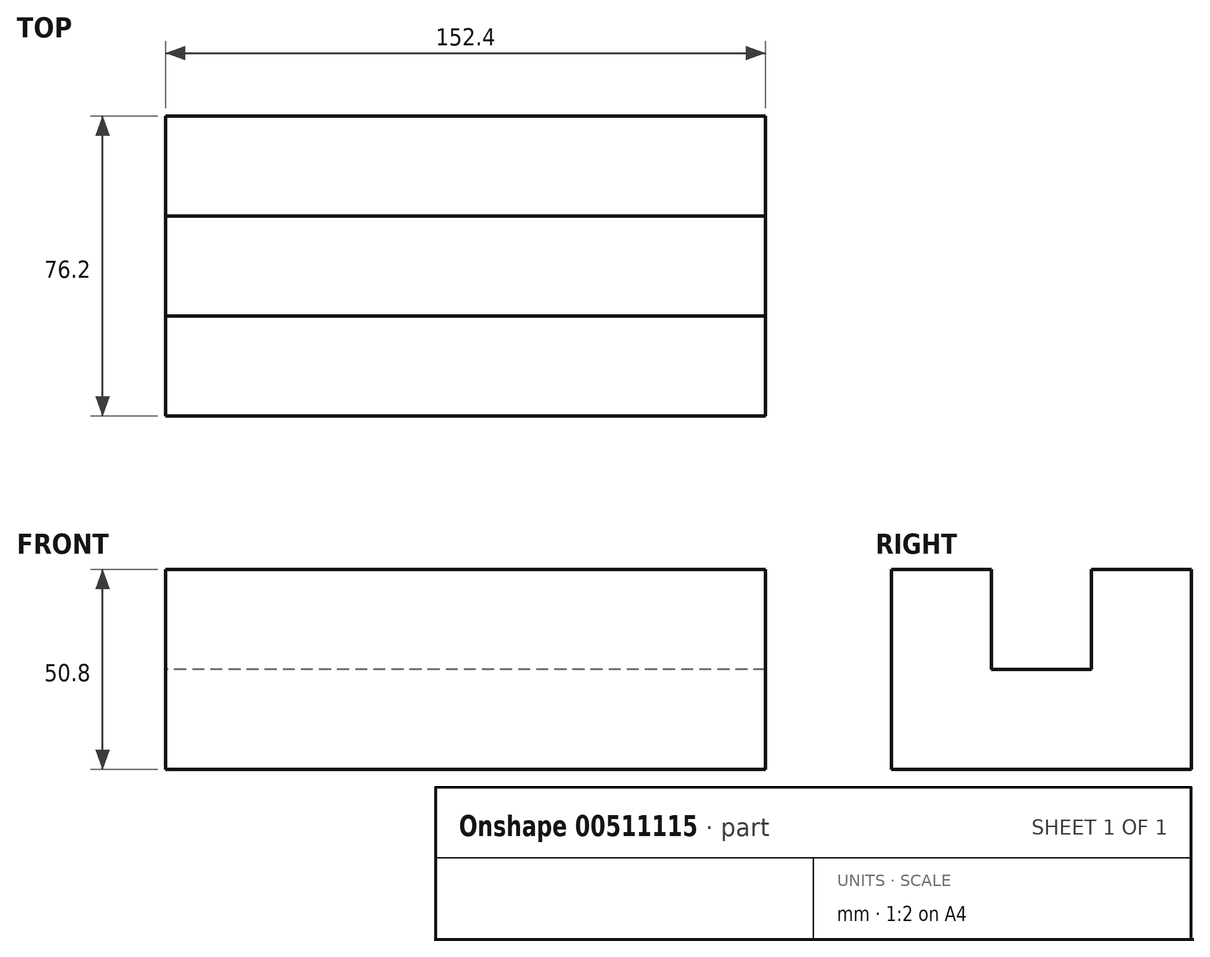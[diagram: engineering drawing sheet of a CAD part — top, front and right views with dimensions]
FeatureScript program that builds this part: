
annotation { "Feature Type Name" : "Feature", "Feature Type Description" : "" }
export const myFeature = defineFeature(function(context is Context, id is Id, definition is map)
    precondition{}
    {
        {
            var Q0;
            Q0=qCreatedBy(makeId("Right.planeOp"),FACE);
            var sketch = newSketch(context, id + "F0", { "sketchPlane" : qUnion([Q0])});
            skLineSegment(sketch, "E0", {"start": v(-40.6, 57.32) * mm, "end": v(-40.6, 6.52) * mm});
            skLineSegment(sketch, "E1", {"start": v(-40.6, 6.52) * mm, "end": v(35.6, 6.52) * mm});
            skLineSegment(sketch, "E2", {"start": v(35.6, 6.52) * mm, "end": v(35.6, 57.32) * mm});
            skLineSegment(sketch, "E3", {"start": v(35.6, 57.32) * mm, "end": v(10.2, 57.32) * mm});
            skLineSegment(sketch, "E4", {"start": v(10.2, 57.32) * mm, "end": v(10.2, 31.92) * mm});
            skLineSegment(sketch, "E5", {"start": v(10.2, 31.92) * mm, "end": v(-15.2, 31.92) * mm});
            skLineSegment(sketch, "E6", {"start": v(-15.2, 31.92) * mm, "end": v(-15.2, 57.32) * mm});
            skLineSegment(sketch, "E7", {"start": v(-15.2, 57.32) * mm, "end": v(-40.6, 57.32) * mm});
            skSolve(sketch);
        }
        {
            var Q0;
            Q0 = qSketchRegion(id + "F0", true);
            extrude(context, id + "F1", {"entities" : qUnion([Q0]), "depth" : 152.4 * mm});
        }
    });
